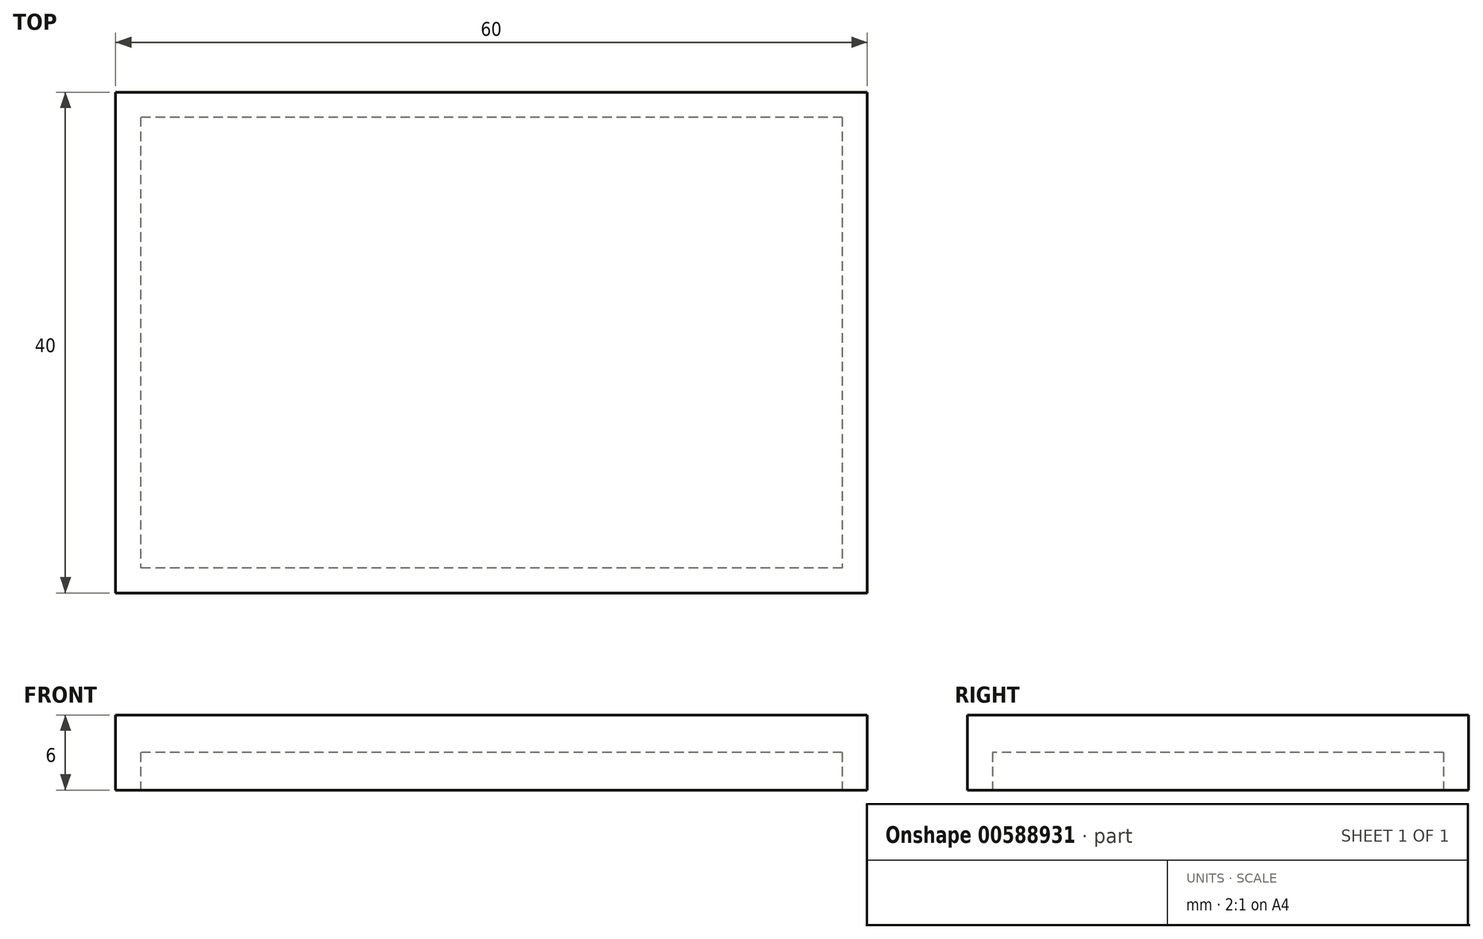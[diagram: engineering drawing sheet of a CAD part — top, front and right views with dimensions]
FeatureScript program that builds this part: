
annotation { "Feature Type Name" : "Feature", "Feature Type Description" : "" }
export const myFeature = defineFeature(function(context is Context, id is Id, definition is map)
    precondition{}
    {
        {
            var Q0;
            Q0=qCreatedBy(makeId("Top.planeOp"),FACE);
            var sketch = newSketch(context, id + "F0", { "sketchPlane" : qUnion([Q0])});
            skLineSegment(sketch, "E0.bottom", {"start": v(-30, 20) * mm, "end": v(30, 20) * mm});
            skLineSegment(sketch, "E0.top", {"start": v(-30, -20) * mm, "end": v(30, -20) * mm});
            skLineSegment(sketch, "E0.left", {"start": v(-30, 20) * mm, "end": v(-30, -20) * mm});
            skLineSegment(sketch, "E0.right", {"start": v(30, 20) * mm, "end": v(30, -20) * mm});
            skPoint(sketch, "E0.middle", {"position": v(0, 0) * mm});
            skSolve(sketch);
        }
        {
            var Q0;
            Q0=makeQuery(id+"F0.imprint","IMPRINT",FACE,{"disambiguationData":[TD([[makeQuery(id+"F0.imprint","IMPRINT",EDGE,{"derivedFrom":sQuery(id+"F0.wireOp",EDGE,"E0.bottom")}),-1.0]])]});
            extrude(context, id + "F1", {"entities" : qUnion([Q0]), "depth" : 6 * mm, "offsetDistance" : 25 * mm, "symmetric" : true});
        }
        {
            var Q0;
            Q0=makeQuery(id+"F1.opExtrude","CAP_FACE",FACE,{"disambiguationData":[OSD([sQuery(id+"F0.wireOp",EDGE,"E0.bottom"),sQuery(id+"F0.wireOp",EDGE,"E0.top"),sQuery(id+"F0.wireOp",EDGE,"E0.left"),sQuery(id+"F0.wireOp",EDGE,"E0.right")])],"isStart":true});
            var sketch = newSketch(context, id + "F2", { "sketchPlane" : qUnion([Q0])});
            skLineSegment(sketch, "E1.bottom", {"start": v(28, -18) * mm, "end": v(-28, -18) * mm});
            skLineSegment(sketch, "E1.top", {"start": v(28, 18) * mm, "end": v(-28, 18) * mm});
            skLineSegment(sketch, "E1.left", {"start": v(28, -18) * mm, "end": v(28, 18) * mm});
            skLineSegment(sketch, "E1.right", {"start": v(-28, -18) * mm, "end": v(-28, 18) * mm});
            skPoint(sketch, "E1.middle", {"position": v(0, 0) * mm});
            skSolve(sketch);
        }
        {
            var Q0;
            Q0=makeQuery(id+"F2.imprint","IMPRINT",FACE,{"disambiguationData":[TD([[makeQuery(id+"F2.imprint","IMPRINT",EDGE,{"derivedFrom":sQuery(id+"F2.wireOp",EDGE,"E1.bottom")}),-1.0]])]});
            extrude(context, id + "F3", {"entities" : qUnion([Q0]), "operationType" : NewBodyOperationType.REMOVE, "oppositeDirection" : true, "depth" : 3 * mm, "offsetDistance" : 25 * mm});
        }
    });
